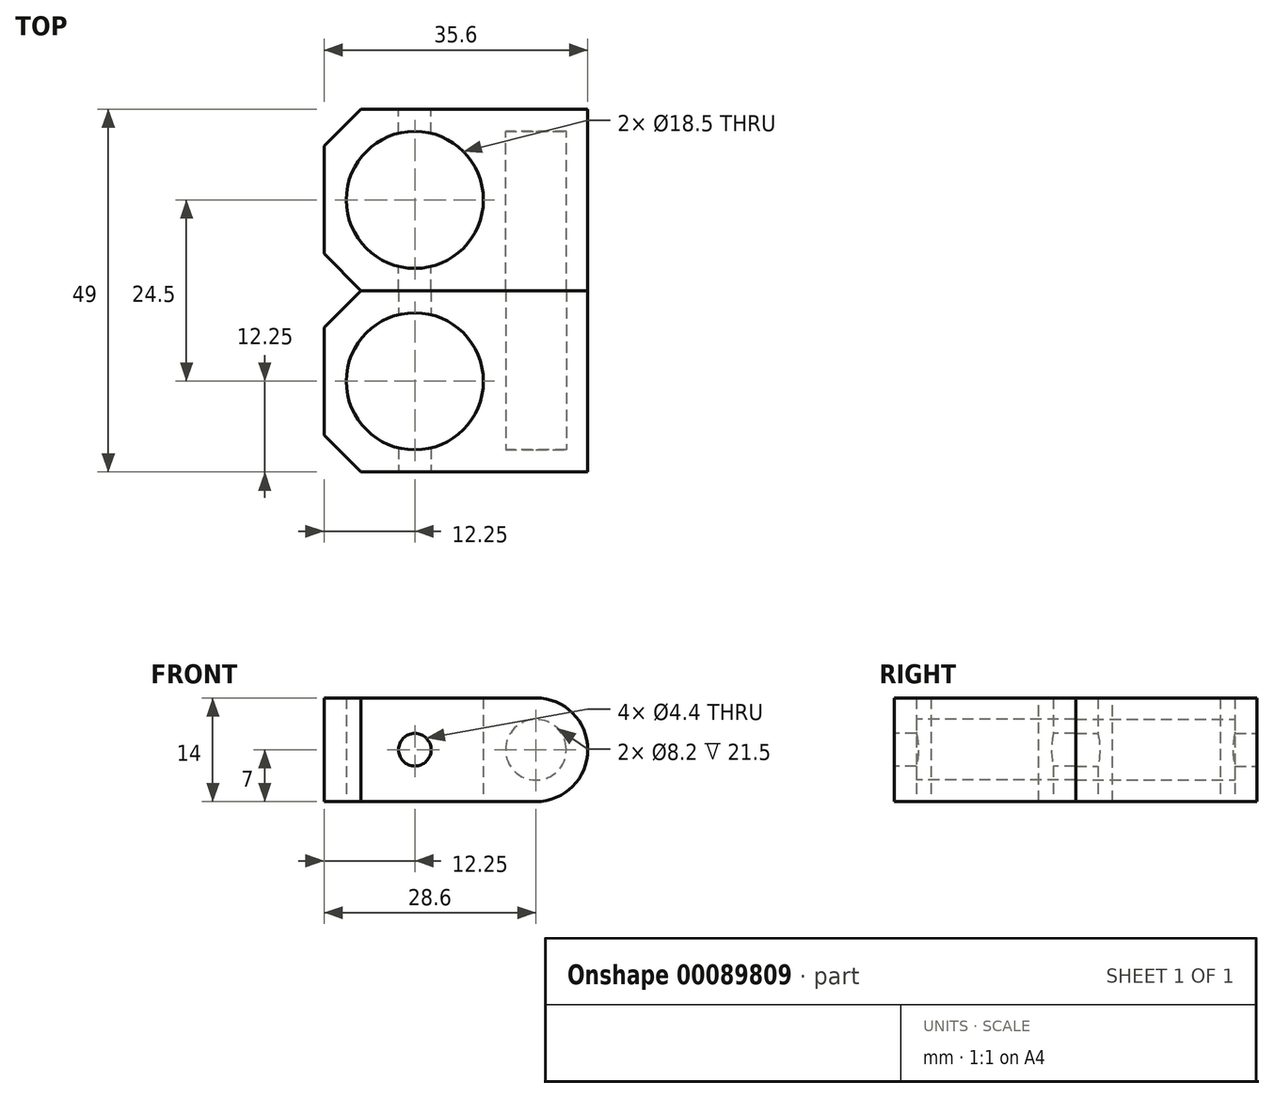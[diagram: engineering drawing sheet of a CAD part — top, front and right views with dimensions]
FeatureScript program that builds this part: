
annotation { "Feature Type Name" : "Feature", "Feature Type Description" : "" }
export const myFeature = defineFeature(function(context is Context, id is Id, definition is map)
    precondition{}
    {
        {
            var Q0;
            Q0=qCreatedBy(makeId("Top.planeOp"),FACE);
            var sketch = newSketch(context, id + "F0", { "sketchPlane" : qUnion([Q0])});
            skCircle(sketch, "E0", {"center": v(0, 0) * mm, "radius": 9.25 * mm});
            skLineSegment(sketch, "E1.bottom", {"start": v(-12.25, 12.25) * mm, "end": v(12.25, 12.25) * mm});
            skLineSegment(sketch, "E1.top", {"start": v(-12.25, -12.25) * mm, "end": v(12.25, -12.25) * mm});
            skLineSegment(sketch, "E1.left", {"start": v(-12.25, 12.25) * mm, "end": v(-12.25, -12.25) * mm});
            skLineSegment(sketch, "E1.right", {"start": v(12.25, 12.25) * mm, "end": v(12.25, -12.25) * mm});
            skSolve(sketch);
        }
        {
            var Q0;
            Q0=makeQuery(id+"F0.imprint","IMPRINT",FACE,{"disambiguationData":[TD([[makeQuery(id+"F0.imprint","IMPRINT",EDGE,{"derivedFrom":sQuery(id+"F0.wireOp",EDGE,"E0")}),-1.0]])]});
            extrude(context, id + "F1", {"entities" : qUnion([Q0]), "depth" : (8 + 3 + 3) * mm});
        }
        {
            var Q0;
            Q0=makeQuery(id+"F1.opExtrude","SWEPT_FACE",FACE,{"disambiguationData":[OSD([sQuery(id+"F0.wireOp",EDGE,"E1.bottom")])]});
            var sketch = newSketch(context, id + "F2", { "sketchPlane" : qUnion([Q0])});
            skCircle(sketch, "E2", {"center": v(0, 7) * mm, "radius": 2.2 * mm});
            skPoint(sketch, "E2.centerSnap0", {"position": v(12.25, 7) * mm});
            skPoint(sketch, "E2.centerSnap1", {"position": v(0, 14) * mm});
            skLineSegment(sketch, "E3.0", {"start": v(-12.25, 14) * mm, "end": v(-12.25, 0) * mm});
            skCircle(sketch, "E4", {"center": v(-16.35, 7) * mm, "radius": 4.1 * mm});
            skPoint(sketch, "E4.centerSnap0", {"position": v(-12.25, 7) * mm});
            skArc(sketch, "E5", {"start": v(-16.35, 14) * mm, "mid": v(-23.35, 7) * mm, "end": v(-16.35, 0) * mm});
            skLineSegment(sketch, "E6", {"start": v(-16.35, 14) * mm, "end": v(-12.25, 14) * mm});
            skLineSegment(sketch, "E7", {"start": v(-16.35, 0) * mm, "end": v(-12.25, 0) * mm});
            skSolve(sketch);
        }
        {
            var Q0;
            Q0=makeQuery(id+"F2.imprint","IMPRINT",FACE,{"disambiguationData":[TD([[makeQuery(id+"F2.imprint","IMPRINT",EDGE,{"derivedFrom":sQuery(id+"F2.wireOp",EDGE,"E2")}),1.0]])]});
            var Q1;
            Q1=makeQuery(id+"F1.opExtrude","SWEPT_FACE",FACE,{"disambiguationData":[OSD([sQuery(id+"F0.wireOp",EDGE,"E1.top")])]});
            extrude(context, id + "F3", {"entities" : qUnion([Q0]), "operationType" : NewBodyOperationType.REMOVE, "endBound" : BoundingType.UP_TO_SURFACE, "oppositeDirection" : true, "endBoundEntityFace" : qUnion([Q1]), "depth" : 25 * mm});
        }
        {
            var Q0;
            {var subQ0=sQuery(id+"F2.wireOp",EDGE,"E4");Q0=makeQuery(id+"F2.imprint","IMPRINT",FACE,{"disambiguationData":[TD([[makeQuery(id+"F2.imprint","IMPRINT",EDGE,{"derivedFrom":subQ0}),-1.0]])]});}
            var Q1;
            Q1=makeQuery(id+"F2.imprint","IMPRINT",FACE,{"disambiguationData":[TD([[makeQuery(id+"F2.imprint","IMPRINT",EDGE,{"derivedFrom":sQuery(id+"F2.wireOp",EDGE,"E4")}),1.0]])]});
            var Q2;
            Q2=makeQuery(id+"F1.opExtrude","SWEPT_FACE",FACE,{"disambiguationData":[OSD([sQuery(id+"F0.wireOp",EDGE,"E1.top")])]});
            extrude(context, id + "F4", {"entities" : qUnion([Q0, Q1]), "operationType" : NewBodyOperationType.ADD, "endBound" : BoundingType.UP_TO_SURFACE, "oppositeDirection" : true, "endBoundEntityFace" : qUnion([Q2]), "depth" : 25 * mm});
        }
        {
            var Q0;
            Q0=makeQuery(id+"F2.imprint","IMPRINT",FACE,{"disambiguationData":[TD([[makeQuery(id+"F2.imprint","IMPRINT",EDGE,{"derivedFrom":sQuery(id+"F2.wireOp",EDGE,"E4")}),1.0]])]});
            var Q1;
            {var subQ0=sQuery(id+"F0.wireOp",EDGE,"E1.top");Q1=makeQuery(id+"F4.boolean.opBoolean","MERGE",FACE,{"derivedFrom":[makeQuery(id+"F1.opExtrude","SWEPT_FACE",FACE,{"disambiguationData":[OSD([subQ0])]}),makeQuery(id+"F4.opExtrude","CAP_FACE",FACE,{"disambiguationData":[OSD([subQ0])],"isStart":false})]});}
            extrude(context, id + "F5", {"entities" : qUnion([Q0]), "operationType" : NewBodyOperationType.REMOVE, "endBound" : BoundingType.UP_TO_SURFACE, "oppositeDirection" : true, "endBoundEntityFace" : qUnion([Q1]), "depth" : 25 * mm, "hasSecondDirection" : true, "secondDirectionOppositeDirection" : true, "secondDirectionDepth" : 3 * mm});
        }
        {
            var Q0;
            Q0=makeQuery(id+"F1.opExtrude","SWEPT_EDGE",EDGE,{"disambiguationData":[OSD([sQuery(id+"F0.wireOp",EDGE,"E1.bottom"),sQuery(id+"F0.wireOp",EDGE,"E1.left")])]});
            var Q1;
            Q1=makeQuery(id+"F1.opExtrude","SWEPT_EDGE",EDGE,{"disambiguationData":[OSD([sQuery(id+"F0.wireOp",EDGE,"E1.top"),sQuery(id+"F0.wireOp",EDGE,"E1.left")])]});
            chamfer(context, id + "F6", {"entities" : qUnion([Q0, Q1]), "width" : 5 * mm, "tangentPropagation" : true});
        }
        {
            var Q0;
            Q0=makeQuery(id+"F1.opExtrude","SWEPT_BODY",BODY,{"disambiguationData":[OSD([sQuery(id+"F0.wireOp",EDGE,"E0"),sQuery(id+"F0.wireOp",EDGE,"E1.bottom"),sQuery(id+"F0.wireOp",EDGE,"E1.top"),sQuery(id+"F0.wireOp",EDGE,"E1.left"),sQuery(id+"F0.wireOp",EDGE,"E1.right")])]});
            var Q1;
            {var subQ0=sQuery(id+"F0.wireOp",EDGE,"E1.top");Q1=makeQuery(id+"F4.boolean.opBoolean","MERGE",FACE,{"derivedFrom":[makeQuery(id+"F1.opExtrude","SWEPT_FACE",FACE,{"disambiguationData":[OSD([subQ0])]}),makeQuery(id+"F4.opExtrude","CAP_FACE",FACE,{"disambiguationData":[OSD([subQ0])],"isStart":false})]});}
            mirror(context, id + "F7", {"entities" : qUnion([Q0]), "mirrorPlane" : qUnion([Q1])});
        }
    });
